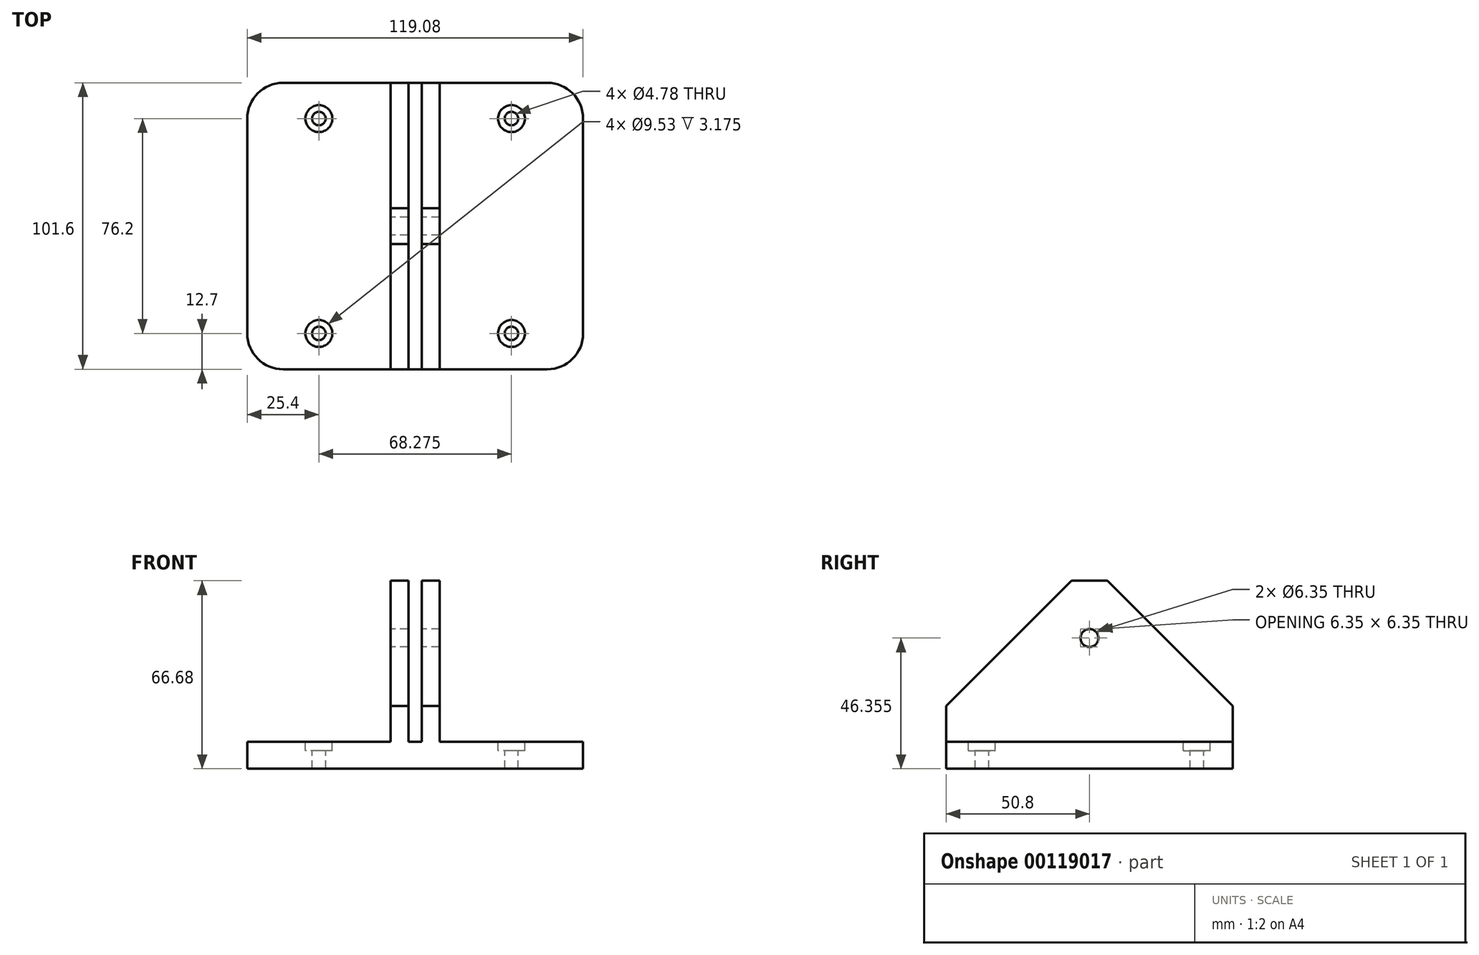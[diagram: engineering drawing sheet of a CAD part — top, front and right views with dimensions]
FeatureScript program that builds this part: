
annotation { "Feature Type Name" : "Feature", "Feature Type Description" : "" }
export const myFeature = defineFeature(function(context is Context, id is Id, definition is map)
    precondition{}
    {
        {
            var Q0;
            Q0=qCreatedBy(makeId("Front.planeOp"),FACE);
            var sketch = newSketch(context, id + "F0", { "sketchPlane" : qUnion([Q0])});
            skLineSegment(sketch, "E0", {"start": v(0, 0) * mm, "end": v(0, 9.53) * mm});
            skLineSegment(sketch, "E1", {"start": v(0, 9.53) * mm, "end": v(50.8, 9.53) * mm});
            skLineSegment(sketch, "E2", {"start": v(50.8, 9.53) * mm, "end": v(50.8, 66.68) * mm});
            skLineSegment(sketch, "E3", {"start": v(50.8, 66.68) * mm, "end": v(57.15, 66.68) * mm});
            skLineSegment(sketch, "E4", {"start": v(57.15, 66.68) * mm, "end": v(57.15, 9.52) * mm});
            skLineSegment(sketch, "E5", {"start": v(57.15, 9.52) * mm, "end": v(61.93, 9.52) * mm});
            skLineSegment(sketch, "E6", {"start": v(61.93, 9.52) * mm, "end": v(61.93, 66.67) * mm});
            skLineSegment(sketch, "E7", {"start": v(61.93, 66.67) * mm, "end": v(68.28, 66.67) * mm});
            skLineSegment(sketch, "E8", {"start": v(68.28, 66.67) * mm, "end": v(68.28, 9.52) * mm});
            skLineSegment(sketch, "E9", {"start": v(68.28, 9.52) * mm, "end": v(119.08, 9.53) * mm});
            skLineSegment(sketch, "E10", {"start": v(119.08, 9.53) * mm, "end": v(119.08, 0) * mm});
            skLineSegment(sketch, "E11", {"start": v(0, 0) * mm, "end": v(119.08, 0) * mm});
            skSolve(sketch);
        }
        {
            var Q0;
            Q0 = qSketchRegion(id + "F0", true);
            extrude(context, id + "F1", {"entities" : qUnion([Q0]), "depth" : 101.6 * mm});
        }
        {
            var Q0;
            Q0=makeQuery(id+"F1.opExtrude","SWEPT_FACE",FACE,{"disambiguationData":[OSD([sQuery(id+"F0.wireOp",EDGE,"E1")])]});
            var sketch = newSketch(context, id + "F2", { "sketchPlane" : qUnion([Q0])});
            skPoint(sketch, "E12", {"position": v(25.4, -12.7) * mm});
            skPoint(sketch, "E12.positionSnap0", {"position": v(25.4, 0) * mm});
            skPoint(sketch, "E13", {"position": v(25.4, -88.9) * mm});
            skSolve(sketch);
        }
        {
            var Q0;
            Q0=sQuery(id+"F2.wireOp",VERTEX,"E12");
            var Q1;
            Q1=sQuery(id+"F2.wireOp",VERTEX,"E13");
            var Q2;
            Q2=makeQuery(id+"F1.opExtrude","SWEPT_BODY",BODY,{"disambiguationData":[OSD([sQuery(id+"F0.wireOp",EDGE,"E0"),sQuery(id+"F0.wireOp",EDGE,"E1"),sQuery(id+"F0.wireOp",EDGE,"E2"),sQuery(id+"F0.wireOp",EDGE,"E3"),sQuery(id+"F0.wireOp",EDGE,"E4"),sQuery(id+"F0.wireOp",EDGE,"E5"),sQuery(id+"F0.wireOp",EDGE,"E6"),sQuery(id+"F0.wireOp",EDGE,"E7"),sQuery(id+"F0.wireOp",EDGE,"E8"),sQuery(id+"F0.wireOp",EDGE,"E9"),sQuery(id+"F0.wireOp",EDGE,"E10"),sQuery(id+"F0.wireOp",EDGE,"E11")])]});
            hole(context, id + "F3", {"style" : HoleStyle.C_BORE, "endStyle" : HoleEndStyle.THROUGH, "holeDiameter" : 4.78 * mm, "cBoreDiameter" : 9.52 * mm, "cBoreDepth" : 3.17 * mm, "locations" : qUnion([Q0, Q1]), "scope" : qUnion([Q2]), "isTappedThrough" : true});
        }
        {
            var Q0;
            Q0=makeQuery(id+"F1.opExtrude","SWEPT_FACE",FACE,{"disambiguationData":[OSD([sQuery(id+"F0.wireOp",EDGE,"E9")])]});
            var sketch = newSketch(context, id + "F4", { "sketchPlane" : qUnion([Q0])});
            skPoint(sketch, "E14", {"position": v(93.68, -12.7) * mm});
            skPoint(sketch, "E14.positionSnap0", {"position": v(93.68, 0) * mm});
            skPoint(sketch, "E15", {"position": v(93.68, -88.9) * mm});
            skSolve(sketch);
        }
        {
            var Q0;
            Q0=sQuery(id+"F4.wireOp",VERTEX,"E14");
            var Q1;
            Q1=sQuery(id+"F4.wireOp",VERTEX,"E15");
            var Q2;
            Q2=makeQuery(id+"F1.opExtrude","SWEPT_BODY",BODY,{"disambiguationData":[OSD([sQuery(id+"F0.wireOp",EDGE,"E0"),sQuery(id+"F0.wireOp",EDGE,"E1"),sQuery(id+"F0.wireOp",EDGE,"E2"),sQuery(id+"F0.wireOp",EDGE,"E3"),sQuery(id+"F0.wireOp",EDGE,"E4"),sQuery(id+"F0.wireOp",EDGE,"E5"),sQuery(id+"F0.wireOp",EDGE,"E6"),sQuery(id+"F0.wireOp",EDGE,"E7"),sQuery(id+"F0.wireOp",EDGE,"E8"),sQuery(id+"F0.wireOp",EDGE,"E9"),sQuery(id+"F0.wireOp",EDGE,"E10"),sQuery(id+"F0.wireOp",EDGE,"E11")])]});
            hole(context, id + "F5", {"style" : HoleStyle.C_BORE, "endStyle" : HoleEndStyle.THROUGH, "holeDiameter" : 4.78 * mm, "cBoreDiameter" : 9.52 * mm, "cBoreDepth" : 3.17 * mm, "locations" : qUnion([Q0, Q1]), "scope" : qUnion([Q2]), "isTappedThrough" : true});
        }
        {
            var Q0;
            Q0=makeQuery(id+"F1.opExtrude","SWEPT_FACE",FACE,{"disambiguationData":[OSD([sQuery(id+"F0.wireOp",EDGE,"E2")])]});
            var sketch = newSketch(context, id + "F6", { "sketchPlane" : qUnion([Q0])});
            skPoint(sketch, "E16", {"position": v(50.8, 46.36) * mm});
            skPoint(sketch, "E16.positionSnap0", {"position": v(50.8, 9.53) * mm});
            skSolve(sketch);
        }
        {
            var Q0;
            Q0=sQuery(id+"F6.wireOp",VERTEX,"E16");
            var Q1;
            Q1=makeQuery(id+"F1.opExtrude","SWEPT_BODY",BODY,{"disambiguationData":[OSD([sQuery(id+"F0.wireOp",EDGE,"E0"),sQuery(id+"F0.wireOp",EDGE,"E1"),sQuery(id+"F0.wireOp",EDGE,"E2"),sQuery(id+"F0.wireOp",EDGE,"E3"),sQuery(id+"F0.wireOp",EDGE,"E4"),sQuery(id+"F0.wireOp",EDGE,"E5"),sQuery(id+"F0.wireOp",EDGE,"E6"),sQuery(id+"F0.wireOp",EDGE,"E7"),sQuery(id+"F0.wireOp",EDGE,"E8"),sQuery(id+"F0.wireOp",EDGE,"E9"),sQuery(id+"F0.wireOp",EDGE,"E10"),sQuery(id+"F0.wireOp",EDGE,"E11")])]});
            hole(context, id + "F7", {"style" : HoleStyle.SIMPLE, "endStyle" : HoleEndStyle.THROUGH, "holeDiameter" : 6.35 * mm, "locations" : qUnion([Q0]), "scope" : qUnion([Q1]), "isTappedThrough" : true});
        }
        {
            var Q0;
            Q0=makeQuery(id+"F1.opExtrude","CAP_EDGE",EDGE,{"disambiguationData":[OSD([sQuery(id+"F0.wireOp",EDGE,"E3")])],"isStart":false});
            var Q1;
            Q1=makeQuery(id+"F1.opExtrude","CAP_EDGE",EDGE,{"disambiguationData":[OSD([sQuery(id+"F0.wireOp",EDGE,"E7")])],"isStart":false});
            var Q2;
            Q2=makeQuery(id+"F1.opExtrude","CAP_EDGE",EDGE,{"disambiguationData":[OSD([sQuery(id+"F0.wireOp",EDGE,"E3")])],"isStart":true});
            var Q3;
            Q3=makeQuery(id+"F1.opExtrude","CAP_EDGE",EDGE,{"disambiguationData":[OSD([sQuery(id+"F0.wireOp",EDGE,"E7")])],"isStart":true});
            chamfer(context, id + "F8", {"entities" : qUnion([Q0, Q1, Q2, Q3]), "width" : 44.45 * mm, "tangentPropagation" : true});
        }
        {
            var Q0;
            Q0=makeQuery(id+"F1.opExtrude","CAP_EDGE",EDGE,{"disambiguationData":[OSD([sQuery(id+"F0.wireOp",EDGE,"E0")])],"isStart":true});
            var Q1;
            Q1=makeQuery(id+"F1.opExtrude","CAP_EDGE",EDGE,{"disambiguationData":[OSD([sQuery(id+"F0.wireOp",EDGE,"E0")])],"isStart":false});
            var Q2;
            Q2=makeQuery(id+"F1.opExtrude","CAP_EDGE",EDGE,{"disambiguationData":[OSD([sQuery(id+"F0.wireOp",EDGE,"E10")])],"isStart":false});
            var Q3;
            Q3=makeQuery(id+"F1.opExtrude","CAP_EDGE",EDGE,{"disambiguationData":[OSD([sQuery(id+"F0.wireOp",EDGE,"E10")])],"isStart":true});
            fillet(context, id + "F9", {"entities" : qUnion([Q0, Q1, Q2, Q3]), "radius" : 12.7 * mm, "tangentPropagation" : true, "allowEdgeOverflow" : false});
        }
    });
